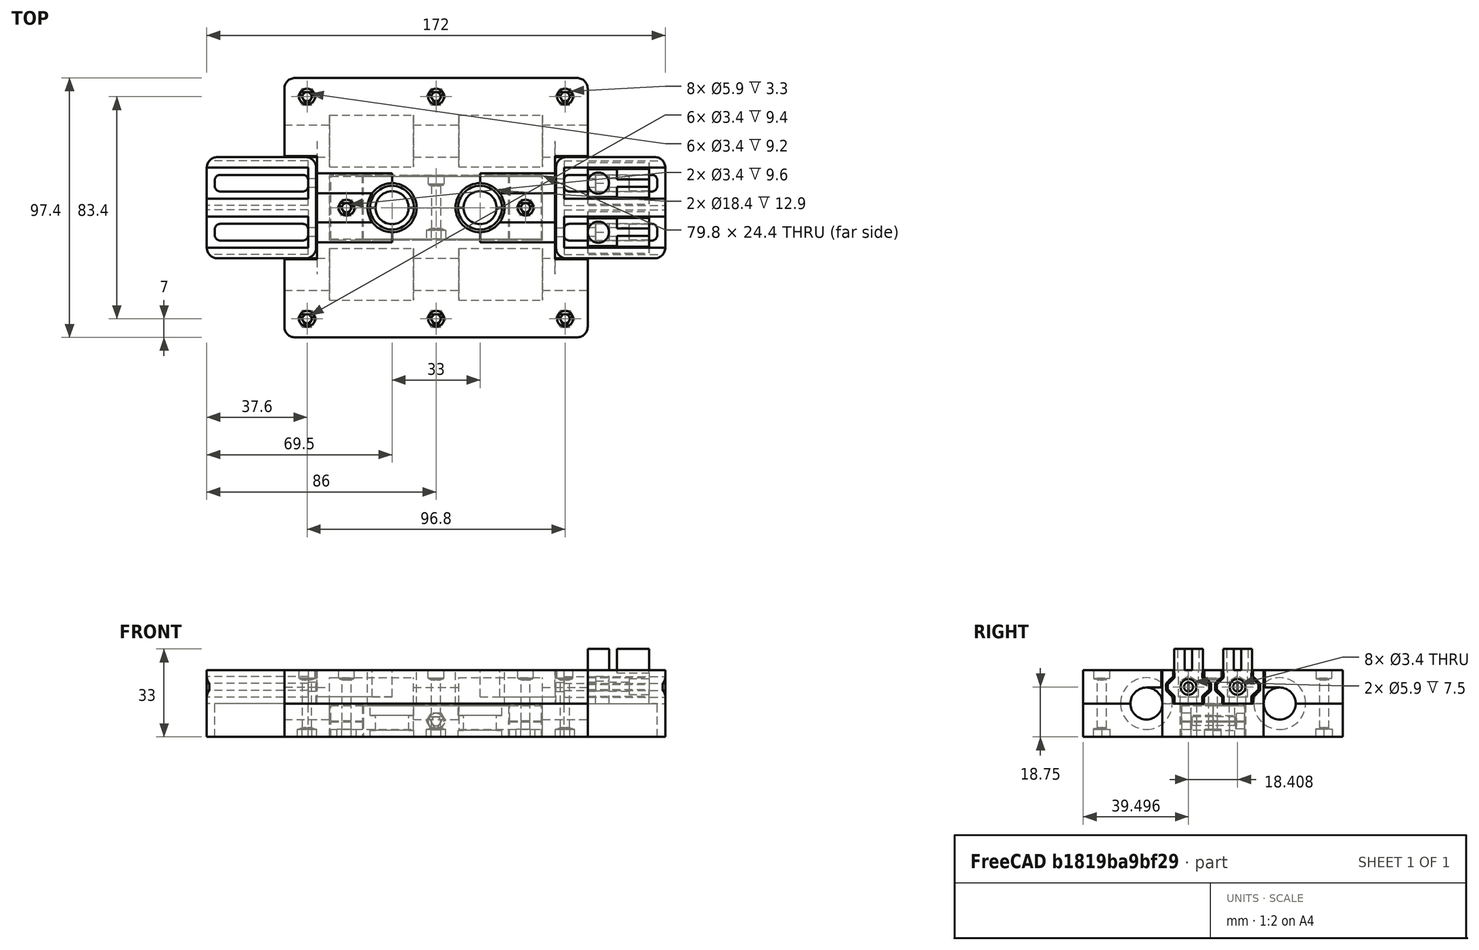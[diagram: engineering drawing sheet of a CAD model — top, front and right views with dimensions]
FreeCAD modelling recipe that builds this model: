
FCSTD DOCUMENT  (FreeCAD 0.16R6706 (Git))
Label: carriage
License: All rights reserved
LicenseURL: http://en.wikipedia.org/wiki/All_rights_reserved
objects: Part::Prism×50, Part::Cylinder×49, Part::MultiFuse×35, Part::Box×27, Part::Common×16, Part::Cut×9, Part::Fillet×5, Part::Fuse×4, Part::Polygon×4, Part::Extrusion×4, Part::FeaturePython×4
note: 207 computed .brp shape members not serialized (recipe doc carries the construction recipe); baked Part::Feature solids carry a one-line shape summary decoded from their .brp

FEATURE [Part::Cylinder] extr_outup
  Angle = 360
  Height = 3.7
  Placement = pos=(0,0,8) rot=(0,0,1;0rad)
  Radius = 8.2
FEATURE [Part::Cylinder] extr_outup_2
  Angle = 360
  Height = 3.7
  Placement = pos=(0,0,8) rot=(0,0,1;0rad)
  Radius = 8.2
FEATURE [Part::Cylinder] extr_in
  Angle = 360
  Height = 5.6
  Placement = pos=(0,0,2.4) rot=(0,0,1;0rad)
  Radius = 6.2
FEATURE [Part::Cylinder] extr_in_2
  Angle = 360
  Height = 5.6
  Placement = pos=(0,0,2.4) rot=(0,0,1;0rad)
  Radius = 6.2
FEATURE [Part::Cylinder] extr_outbot
  Angle = 360
  Height = 3.4
  Placement = pos=(0,0,-1) rot=(0,0,1;0rad)
  Radius = 8.2
FEATURE [Part::Cylinder] extr_outbot_2
  Angle = 360
  Height = 3.4
  Placement = pos=(0,0,-1) rot=(0,0,1;0rad)
  Radius = 8.2
FEATURE [Part::MultiFuse] extr_rings_1
  Placement = pos=(16.5,0,0) rot=(0,0,1;0rad)
  Shapes = -> [extr_outup,extr_in,extr_outbot]
FEATURE [Part::MultiFuse] extr_rings_2
  Placement = pos=(-16.5,0,0) rot=(0,0,1;0rad)
  Shapes = -> [extr_outup_2,extr_in_2,extr_outbot_2]
FEATURE [Part::Box] extr_hold_1
  Height = 11.7
  Length = 79
  Placement = pos=(-39.5,0,0) rot=(0,0,1;0rad)
  Width = 11.8
FEATURE [Part::Box] extr_hold_2
  Height = 11.7
  Length = 79
  Placement = pos=(-39.5,-11.8,0) rot=(0,0,1;0rad)
  Width = 11.8
FEATURE [Part::Box] extr_hold_tab0
  Height = 5.65
  Length = 11.84
  Placement = pos=(-39.5,-1,6.05) rot=(0,0,1;0rad)
  Width = 12.8
FEATURE [Part::Box] extr_hold_tab0_hole
  Height = 7.05
  Length = 13.24
  Placement = pos=(-40.5,0,5.65) rot=(0,0,1;0rad)
  Width = 12.8
FEATURE [Part::Box] extr_hold_tab1
  Height = 5.65
  Length = 11.84
  Placement = pos=(-39.5,-11.8,0) rot=(0,0,1;0rad)
  Width = 12.8
FEATURE [Part::Box] extr_hold_tab1_hole
  Height = 7.05
  Length = 13.24
  Placement = pos=(-40.5,-12.8,-1) rot=(0,0,1;0rad)
  Width = 12.8
FEATURE [Part::Box] extr_hold_tab2
  Height = 5.65
  Length = 11.84
  Placement = pos=(27.66,-11.8,6.05) rot=(0,0,1;0rad)
  Width = 12.8
FEATURE [Part::Box] extr_hold_tab2_hole
  Height = 7.05
  Length = 13.24
  Placement = pos=(27.26,-12.8,5.65) rot=(0,0,1;0rad)
  Width = 12.8
FEATURE [Part::Box] extr_hold_tab3
  Height = 5.65
  Length = 11.84
  Placement = pos=(27.66,-1,0) rot=(0,0,1;0rad)
  Width = 12.8
FEATURE [Part::Box] extr_hold_tab3_hole
  Height = 7.05
  Length = 13.24
  Placement = pos=(27.26,0,-1) rot=(0,0,1;0rad)
  Width = 12.8
FEATURE [Part::MultiFuse] extr_hold1_holes_joint
  Shapes = -> [extr_hold_tab0_hole,extr_hold_tab3_hole]
FEATURE [Part::MultiFuse] extr_hold1_tabs_joint
  Shapes = -> [extr_hold_1,extr_hold_tab1,extr_hold_tab2]
FEATURE [Part::Cut] extr_hold1_joint
  Base = -> extr_hold1_tabs_joint
  Tool = -> extr_hold1_holes_joint
FEATURE [Part::MultiFuse] extr_hold2_holes_joint
  Shapes = -> [extr_hold_tab1_hole,extr_hold_tab2_hole]
FEATURE [Part::MultiFuse] extr_hold2_tabs_joint
  Shapes = -> [extr_hold_2,extr_hold_tab0,extr_hold_tab3]
FEATURE [Part::Cut] extr_hold2_joint
  Base = -> extr_hold2_tabs_joint
  Tool = -> extr_hold2_holes_joint
FEATURE [Part::Box] carlow_box
  Height = 12.5
  Length = 113.8
  Placement = pos=(-56.9,-48.7,0) rot=(0,0,1;0rad)
  Width = 97.4
FEATURE [Part::Fillet] carlow_box_fllt
  Base = -> carlow_box
  Edges = 4 edges r=4: [Edge1,Edge3,Edge5,Edge7]
FEATURE [Part::Box] carhig_box
  Height = 12.5
  Length = 113.8
  Placement = pos=(-56.9,-48.7,0) rot=(0,0,1;0rad)
  Width = 97.4
FEATURE [Part::Fillet] carhig_box_fllt
  Base = -> carhig_box
  Edges = 4 edges r=4: [Edge1,Edge3,Edge5,Edge7]
  Placement = pos=(0,0,12.5) rot=(0,0,1;0rad)
FEATURE [Part::Box] inrect
  Height = 14.5
  Length = 79.8
  Placement = pos=(-39.9,-12.2,-1) rot=(0,0,1;0rad)
  Width = 24.4
FEATURE [Part::Box] extrhold_higcar
  Height = 1.4
  Length = 79
  Placement = pos=(-39.5,-11.8,12.1) rot=(0,0,1;0rad)
  Width = 23.6
FEATURE [Part::Fuse] carghig_fuse
  Base = -> carhig_box_fllt
  Tool = -> extrhold_higcar
FEATURE [Part::Cylinder] rod_p
  Angle = 360
  Height = 115.8
  Placement = pos=(-57.9,25,12.5) rot=(0,1,0;1.5708rad)
  Radius = 6
FEATURE [Part::Cylinder] rod_n
  Angle = 360
  Height = 115.8
  Placement = pos=(-57.9,-25,12.5) rot=(0,1,0;1.5708rad)
  Radius = 6
FEATURE [Part::Cylinder] bearing_0
  Angle = 360
  Height = 31.4
  Placement = pos=(8.5,25,12.5) rot=(0,1,0;1.5708rad)
  Radius = 9.7
FEATURE [Part::Cylinder] bearing_1
  Angle = 360
  Height = 31.4
  Placement = pos=(-39.9,25,12.5) rot=(0,1,0;1.5708rad)
  Radius = 9.7
FEATURE [Part::Cylinder] bearing_2
  Angle = 360
  Height = 31.4
  Placement = pos=(8.5,-25,12.5) rot=(0,1,0;1.5708rad)
  Radius = 9.7
FEATURE [Part::Cylinder] bearing_3
  Angle = 360
  Height = 31.4
  Placement = pos=(-39.9,-25,12.5) rot=(0,1,0;1.5708rad)
  Radius = 9.7
FEATURE [Part::Cylinder] higcar_fil_hole1
  Angle = 360
  Height = 15.3
  Placement = pos=(16.5,0,10.7) rot=(0,0,1;0rad)
  Radius = 9.2
FEATURE [Part::Cylinder] higcar_fil_hole2
  Angle = 360
  Height = 15.3
  Placement = pos=(-16.5,0,10.7) rot=(0,0,1;0rad)
  Radius = 9.2
FEATURE [Part::Cylinder] m3_extrbolt_hole_bolt_shank
  Angle = 360
  Height = 25.6
  Placement = pos=(0,0,-1) rot=(0,0,1;0rad)
  Radius = 1.7
FEATURE [Part::Cylinder] m3_extrbolt_hole_bolt_head
  Angle = 360
  Height = 4
  Placement = pos=(0,0,-1) rot=(0,0,1;0rad)
  Radius = 2.95
FEATURE [Part::Prism] m3_extrbolt_hole_bolt_sup1
  Circumradius = 3.4
  Height = 3.3
  Placement = pos=(0,0,0) rot=(0,0,1;0.523599rad)
  Polygon = 3
FEATURE [Part::Cylinder] m3_extrbolt_hole_bolt_sup1away
  Angle = 360
  Height = 3.3
  Radius = 2.95
FEATURE [Part::Common] sup1cut
  Base = -> m3_extrbolt_hole_bolt_sup1
  Tool = -> m3_extrbolt_hole_bolt_sup1away
FEATURE [Part::Prism] m3_extrbolt_hole_bolt_sup2
  Circumradius = 1.955
  Height = 3.6
  Polygon = 6
FEATURE [Part::MultiFuse] m3_extrbolt_hole_bolt
  Shapes = -> [m3_extrbolt_hole_bolt_shank,m3_extrbolt_hole_bolt_head,sup1cut,m3_extrbolt_hole_bolt_sup2]
FEATURE [Part::Prism] m3_extrbolt_hole_nut
  Circumradius = 3.605
  Height = 4.4
  Placement = pos=(0,0,20.2) rot=(0,0,1;0rad)
  Polygon = 6
FEATURE [Part::Prism] m3_extrbolt_hole_nutsup1
  Circumradius = 3.4
  Height = 3.7
  Placement = pos=(0,0,19.9) rot=(0,0,1;0.523599rad)
  Polygon = 3
FEATURE [Part::Prism] m3_extrbolt_hole_supnut1away
  Circumradius = 3.605
  Height = 3.7
  Placement = pos=(0,0,19.9) rot=(0,0,1;0rad)
  Polygon = 6
FEATURE [Part::Common] supnut1_cut
  Base = -> m3_extrbolt_hole_nutsup1
  Tool = -> m3_extrbolt_hole_supnut1away
FEATURE [Part::Prism] m3_extrbolt_hole_supnut2
  Circumradius = 1.955
  Height = 4
  Placement = pos=(0,0,19.6) rot=(0,0,1;0rad)
  Polygon = 6
FEATURE [Part::MultiFuse] boltnut
  Placement = pos=(0,11.8,5.85) rot=(1,0,0;1.5708rad)
  Shapes = -> [m3_extrbolt_hole_bolt,m3_extrbolt_hole_nut,supnut1_cut,m3_extrbolt_hole_supnut2]
FEATURE [Part::Cylinder] m3_bolt_hole_bolt_shank
  Angle = 360
  Height = 27
  Placement = pos=(0,0,-1) rot=(0,0,1;0rad)
  Radius = 1.7
FEATURE [Part::Cylinder] m3_bolt_hole_bolt_head
  Angle = 360
  Height = 4
  Placement = pos=(0,0,22) rot=(0,0,1;0rad)
  Radius = 2.95
FEATURE [Part::Prism] m3_bolt_hole_bolt_sup1
  Circumradius = 3.4
  Height = 3.3
  Placement = pos=(0,0,21.7) rot=(0,0,1;0.523599rad)
  Polygon = 3
FEATURE [Part::Cylinder] m3_bolt_hole_bolt_sup1away
  Angle = 360
  Height = 3.3
  Placement = pos=(0,0,21.7) rot=(0,0,1;0rad)
  Radius = 2.95
FEATURE [Part::Common] sup1cut001
  Base = -> m3_bolt_hole_bolt_sup1
  Tool = -> m3_bolt_hole_bolt_sup1away
FEATURE [Part::Prism] m3_bolt_hole_bolt_sup2
  Circumradius = 1.955
  Height = 3.6
  Placement = pos=(0,0,21.4) rot=(0,0,1;0rad)
  Polygon = 6
FEATURE [Part::MultiFuse] m3_bolt_hole_bolt
  Shapes = -> [m3_bolt_hole_bolt_shank,m3_bolt_hole_bolt_head,sup1cut001,m3_bolt_hole_bolt_sup2]
FEATURE [Part::Prism] m3_bolt_hole_nut
  Circumradius = 3.605
  Height = 3.8
  Placement = pos=(0,0,-1) rot=(0,0,1;0rad)
  Polygon = 6
FEATURE [Part::MultiFuse] boltnut001
  Placement = pos=(33.58,0,0) rot=(0,0,1;0rad)
  Shapes = -> [m3_bolt_hole_bolt,m3_bolt_hole_nut]
FEATURE [Part::Cylinder] m3_bolt_hole_bolt_shank001
  Angle = 360
  Height = 27
  Placement = pos=(0,0,-1) rot=(0,0,1;0rad)
  Radius = 1.7
FEATURE [Part::Cylinder] m3_bolt_hole_bolt_head001
  Angle = 360
  Height = 4
  Placement = pos=(0,0,22) rot=(0,0,1;0rad)
  Radius = 2.95
FEATURE [Part::Prism] m3_bolt_hole_bolt_sup1001
  Circumradius = 3.4
  Height = 3.3
  Placement = pos=(0,0,21.7) rot=(0,0,1;0.523599rad)
  Polygon = 3
FEATURE [Part::Cylinder] m3_bolt_hole_bolt_sup1away001
  Angle = 360
  Height = 3.3
  Placement = pos=(0,0,21.7) rot=(0,0,1;0rad)
  Radius = 2.95
FEATURE [Part::Common] sup1cut002
  Base = -> m3_bolt_hole_bolt_sup1001
  Tool = -> m3_bolt_hole_bolt_sup1away001
FEATURE [Part::Prism] m3_bolt_hole_bolt_sup2001
  Circumradius = 1.955
  Height = 3.6
  Placement = pos=(0,0,21.4) rot=(0,0,1;0rad)
  Polygon = 6
FEATURE [Part::MultiFuse] m3_bolt_hole_bolt001
  Shapes = -> [m3_bolt_hole_bolt_shank001,m3_bolt_hole_bolt_head001,sup1cut002,m3_bolt_hole_bolt_sup2001]
FEATURE [Part::Prism] m3_bolt_hole_nut001
  Circumradius = 3.605
  Height = 3.8
  Placement = pos=(0,0,-1) rot=(0,0,1;0rad)
  Polygon = 6
FEATURE [Part::MultiFuse] boltnut002
  Placement = pos=(-33.58,0,0) rot=(0,0,1;0rad)
  Shapes = -> [m3_bolt_hole_bolt001,m3_bolt_hole_nut001]
FEATURE [Part::Cylinder] m3_bolt_hole_bolt_shank002
  Angle = 360
  Height = 27
  Placement = pos=(0,0,-1) rot=(0,0,1;0rad)
  Radius = 1.7
FEATURE [Part::Cylinder] m3_bolt_hole_bolt_head002
  Angle = 360
  Height = 4
  Placement = pos=(0,0,22) rot=(0,0,1;0rad)
  Radius = 2.95
FEATURE [Part::Prism] m3_bolt_hole_bolt_sup1002
  Circumradius = 3.4
  Height = 3.3
  Placement = pos=(0,0,21.7) rot=(0,0,1;0.523599rad)
  Polygon = 3
FEATURE [Part::Cylinder] m3_bolt_hole_bolt_sup1away002
  Angle = 360
  Height = 3.3
  Placement = pos=(0,0,21.7) rot=(0,0,1;0rad)
  Radius = 2.95
FEATURE [Part::Common] sup1cut003
  Base = -> m3_bolt_hole_bolt_sup1002
  Tool = -> m3_bolt_hole_bolt_sup1away002
FEATURE [Part::Prism] m3_bolt_hole_bolt_sup2002
  Circumradius = 1.955
  Height = 3.6
  Placement = pos=(0,0,21.4) rot=(0,0,1;0rad)
  Polygon = 6
FEATURE [Part::MultiFuse] m3_bolt_hole_bolt002
  Shapes = -> [m3_bolt_hole_bolt_shank002,m3_bolt_hole_bolt_head002,sup1cut003,m3_bolt_hole_bolt_sup2002]
FEATURE [Part::Prism] m3_bolt_hole_nut002
  Circumradius = 3.605
  Height = 3.8
  Placement = pos=(0,0,-1) rot=(0,0,1;0rad)
  Polygon = 6
FEATURE [Part::Prism] m3_bolt_hole_nutsup1
  Circumradius = 3.4
  Height = 3.1
  Placement = pos=(0,0,0) rot=(0,0,1;0.523599rad)
  Polygon = 3
FEATURE [Part::Prism] m3_bolt_hole_supnut1away
  Circumradius = 3.605
  Height = 3.1
  Polygon = 6
FEATURE [Part::Common] supnut1_cut001
  Base = -> m3_bolt_hole_nutsup1
  Tool = -> m3_bolt_hole_supnut1away
FEATURE [Part::Prism] m3_bolt_hole_supnut2
  Circumradius = 1.955
  Height = 3.4
  Polygon = 6
FEATURE [Part::MultiFuse] boltnut003
  Placement = pos=(48.4,41.7,0) rot=(0,0,1;0rad)
  Shapes = -> [m3_bolt_hole_bolt002,m3_bolt_hole_nut002,supnut1_cut001,m3_bolt_hole_supnut2]
FEATURE [Part::Cylinder] m3_bolt_hole_bolt_shank003
  Angle = 360
  Height = 27
  Placement = pos=(0,0,-1) rot=(0,0,1;0rad)
  Radius = 1.7
FEATURE [Part::Cylinder] m3_bolt_hole_bolt_head003
  Angle = 360
  Height = 4
  Placement = pos=(0,0,22) rot=(0,0,1;0rad)
  Radius = 2.95
FEATURE [Part::Prism] m3_bolt_hole_bolt_sup1003
  Circumradius = 3.4
  Height = 3.3
  Placement = pos=(0,0,21.7) rot=(0,0,1;0.523599rad)
  Polygon = 3
FEATURE [Part::Cylinder] m3_bolt_hole_bolt_sup1away003
  Angle = 360
  Height = 3.3
  Placement = pos=(0,0,21.7) rot=(0,0,1;0rad)
  Radius = 2.95
FEATURE [Part::Common] sup1cut004
  Base = -> m3_bolt_hole_bolt_sup1003
  Tool = -> m3_bolt_hole_bolt_sup1away003
FEATURE [Part::Prism] m3_bolt_hole_bolt_sup2003
  Circumradius = 1.955
  Height = 3.6
  Placement = pos=(0,0,21.4) rot=(0,0,1;0rad)
  Polygon = 6
FEATURE [Part::MultiFuse] m3_bolt_hole_bolt003
  Shapes = -> [m3_bolt_hole_bolt_shank003,m3_bolt_hole_bolt_head003,sup1cut004,m3_bolt_hole_bolt_sup2003]
FEATURE [Part::Prism] m3_bolt_hole_nut003
  Circumradius = 3.605
  Height = 3.8
  Placement = pos=(0,0,-1) rot=(0,0,1;0rad)
  Polygon = 6
FEATURE [Part::Prism] m3_bolt_hole_nutsup1001
  Circumradius = 3.4
  Height = 3.1
  Placement = pos=(0,0,0) rot=(0,0,1;0.523599rad)
  Polygon = 3
FEATURE [Part::Prism] m3_bolt_hole_supnut1away001
  Circumradius = 3.605
  Height = 3.1
  Polygon = 6
FEATURE [Part::Common] supnut1_cut002
  Base = -> m3_bolt_hole_nutsup1001
  Tool = -> m3_bolt_hole_supnut1away001
FEATURE [Part::Prism] m3_bolt_hole_supnut2001
  Circumradius = 1.955
  Height = 3.4
  Polygon = 6
FEATURE [Part::MultiFuse] boltnut004
  Placement = pos=(0,41.7,0) rot=(0,0,1;0rad)
  Shapes = -> [m3_bolt_hole_bolt003,m3_bolt_hole_nut003,supnut1_cut002,m3_bolt_hole_supnut2001]
FEATURE [Part::Cylinder] m3_bolt_hole_bolt_shank004
  Angle = 360
  Height = 27
  Placement = pos=(0,0,-1) rot=(0,0,1;0rad)
  Radius = 1.7
FEATURE [Part::Cylinder] m3_bolt_hole_bolt_head004
  Angle = 360
  Height = 4
  Placement = pos=(0,0,22) rot=(0,0,1;0rad)
  Radius = 2.95
FEATURE [Part::Prism] m3_bolt_hole_bolt_sup1004
  Circumradius = 3.4
  Height = 3.3
  Placement = pos=(0,0,21.7) rot=(0,0,1;0.523599rad)
  Polygon = 3
FEATURE [Part::Cylinder] m3_bolt_hole_bolt_sup1away004
  Angle = 360
  Height = 3.3
  Placement = pos=(0,0,21.7) rot=(0,0,1;0rad)
  Radius = 2.95
FEATURE [Part::Common] sup1cut005
  Base = -> m3_bolt_hole_bolt_sup1004
  Tool = -> m3_bolt_hole_bolt_sup1away004
FEATURE [Part::Prism] m3_bolt_hole_bolt_sup2004
  Circumradius = 1.955
  Height = 3.6
  Placement = pos=(0,0,21.4) rot=(0,0,1;0rad)
  Polygon = 6
FEATURE [Part::MultiFuse] m3_bolt_hole_bolt004
  Shapes = -> [m3_bolt_hole_bolt_shank004,m3_bolt_hole_bolt_head004,sup1cut005,m3_bolt_hole_bolt_sup2004]
FEATURE [Part::Prism] m3_bolt_hole_nut004
  Circumradius = 3.605
  Height = 3.8
  Placement = pos=(0,0,-1) rot=(0,0,1;0rad)
  Polygon = 6
FEATURE [Part::Prism] m3_bolt_hole_nutsup1002
  Circumradius = 3.4
  Height = 3.1
  Placement = pos=(0,0,0) rot=(0,0,1;0.523599rad)
  Polygon = 3
FEATURE [Part::Prism] m3_bolt_hole_supnut1away002
  Circumradius = 3.605
  Height = 3.1
  Polygon = 6
FEATURE [Part::Common] supnut1_cut003
  Base = -> m3_bolt_hole_nutsup1002
  Tool = -> m3_bolt_hole_supnut1away002
FEATURE [Part::Prism] m3_bolt_hole_supnut2002
  Circumradius = 1.955
  Height = 3.4
  Polygon = 6
FEATURE [Part::MultiFuse] boltnut005
  Placement = pos=(-48.4,41.7,0) rot=(0,0,1;0rad)
  Shapes = -> [m3_bolt_hole_bolt004,m3_bolt_hole_nut004,supnut1_cut003,m3_bolt_hole_supnut2002]
FEATURE [Part::Cylinder] m3_bolt_hole_bolt_shank005
  Angle = 360
  Height = 27
  Placement = pos=(0,0,-1) rot=(0,0,1;0rad)
  Radius = 1.7
FEATURE [Part::Cylinder] m3_bolt_hole_bolt_head005
  Angle = 360
  Height = 4
  Placement = pos=(0,0,22) rot=(0,0,1;0rad)
  Radius = 2.95
FEATURE [Part::Prism] m3_bolt_hole_bolt_sup1005
  Circumradius = 3.4
  Height = 3.3
  Placement = pos=(0,0,21.7) rot=(0,0,1;0.523599rad)
  Polygon = 3
FEATURE [Part::Cylinder] m3_bolt_hole_bolt_sup1away005
  Angle = 360
  Height = 3.3
  Placement = pos=(0,0,21.7) rot=(0,0,1;0rad)
  Radius = 2.95
FEATURE [Part::Common] sup1cut006
  Base = -> m3_bolt_hole_bolt_sup1005
  Tool = -> m3_bolt_hole_bolt_sup1away005
FEATURE [Part::Prism] m3_bolt_hole_bolt_sup2005
  Circumradius = 1.955
  Height = 3.6
  Placement = pos=(0,0,21.4) rot=(0,0,1;0rad)
  Polygon = 6
FEATURE [Part::MultiFuse] m3_bolt_hole_bolt005
  Shapes = -> [m3_bolt_hole_bolt_shank005,m3_bolt_hole_bolt_head005,sup1cut006,m3_bolt_hole_bolt_sup2005]
FEATURE [Part::Prism] m3_bolt_hole_nut005
  Circumradius = 3.605
  Height = 3.8
  Placement = pos=(0,0,-1) rot=(0,0,1;0rad)
  Polygon = 6
FEATURE [Part::Prism] m3_bolt_hole_nutsup1003
  Circumradius = 3.4
  Height = 3.1
  Placement = pos=(0,0,0) rot=(0,0,1;0.523599rad)
  Polygon = 3
FEATURE [Part::Prism] m3_bolt_hole_supnut1away003
  Circumradius = 3.605
  Height = 3.1
  Polygon = 6
FEATURE [Part::Common] supnut1_cut004
  Base = -> m3_bolt_hole_nutsup1003
  Tool = -> m3_bolt_hole_supnut1away003
FEATURE [Part::Prism] m3_bolt_hole_supnut2003
  Circumradius = 1.955
  Height = 3.4
  Polygon = 6
FEATURE [Part::MultiFuse] boltnut006
  Placement = pos=(48.4,-41.7,0) rot=(0,0,1;0rad)
  Shapes = -> [m3_bolt_hole_bolt005,m3_bolt_hole_nut005,supnut1_cut004,m3_bolt_hole_supnut2003]
FEATURE [Part::Cylinder] m3_bolt_hole_bolt_shank006
  Angle = 360
  Height = 27
  Placement = pos=(0,0,-1) rot=(0,0,1;0rad)
  Radius = 1.7
FEATURE [Part::Cylinder] m3_bolt_hole_bolt_head006
  Angle = 360
  Height = 4
  Placement = pos=(0,0,22) rot=(0,0,1;0rad)
  Radius = 2.95
FEATURE [Part::Prism] m3_bolt_hole_bolt_sup1006
  Circumradius = 3.4
  Height = 3.3
  Placement = pos=(0,0,21.7) rot=(0,0,1;0.523599rad)
  Polygon = 3
FEATURE [Part::Cylinder] m3_bolt_hole_bolt_sup1away006
  Angle = 360
  Height = 3.3
  Placement = pos=(0,0,21.7) rot=(0,0,1;0rad)
  Radius = 2.95
FEATURE [Part::Common] sup1cut007
  Base = -> m3_bolt_hole_bolt_sup1006
  Tool = -> m3_bolt_hole_bolt_sup1away006
FEATURE [Part::Prism] m3_bolt_hole_bolt_sup2006
  Circumradius = 1.955
  Height = 3.6
  Placement = pos=(0,0,21.4) rot=(0,0,1;0rad)
  Polygon = 6
FEATURE [Part::MultiFuse] m3_bolt_hole_bolt006
  Shapes = -> [m3_bolt_hole_bolt_shank006,m3_bolt_hole_bolt_head006,sup1cut007,m3_bolt_hole_bolt_sup2006]
FEATURE [Part::Prism] m3_bolt_hole_nut006
  Circumradius = 3.605
  Height = 3.8
  Placement = pos=(0,0,-1) rot=(0,0,1;0rad)
  Polygon = 6
FEATURE [Part::Prism] m3_bolt_hole_nutsup1004
  Circumradius = 3.4
  Height = 3.1
  Placement = pos=(0,0,0) rot=(0,0,1;0.523599rad)
  Polygon = 3
FEATURE [Part::Prism] m3_bolt_hole_supnut1away004
  Circumradius = 3.605
  Height = 3.1
  Polygon = 6
FEATURE [Part::Common] supnut1_cut005
  Base = -> m3_bolt_hole_nutsup1004
  Tool = -> m3_bolt_hole_supnut1away004
FEATURE [Part::Prism] m3_bolt_hole_supnut2004
  Circumradius = 1.955
  Height = 3.4
  Polygon = 6
FEATURE [Part::MultiFuse] boltnut007
  Placement = pos=(0,-41.7,0) rot=(0,0,1;0rad)
  Shapes = -> [m3_bolt_hole_bolt006,m3_bolt_hole_nut006,supnut1_cut005,m3_bolt_hole_supnut2004]
FEATURE [Part::Cylinder] m3_bolt_hole_bolt_shank007
  Angle = 360
  Height = 27
  Placement = pos=(0,0,-1) rot=(0,0,1;0rad)
  Radius = 1.7
FEATURE [Part::Cylinder] m3_bolt_hole_bolt_head007
  Angle = 360
  Height = 4
  Placement = pos=(0,0,22) rot=(0,0,1;0rad)
  Radius = 2.95
FEATURE [Part::Prism] m3_bolt_hole_bolt_sup1007
  Circumradius = 3.4
  Height = 3.3
  Placement = pos=(0,0,21.7) rot=(0,0,1;0.523599rad)
  Polygon = 3
FEATURE [Part::Cylinder] m3_bolt_hole_bolt_sup1away007
  Angle = 360
  Height = 3.3
  Placement = pos=(0,0,21.7) rot=(0,0,1;0rad)
  Radius = 2.95
FEATURE [Part::Common] sup1cut008
  Base = -> m3_bolt_hole_bolt_sup1007
  Tool = -> m3_bolt_hole_bolt_sup1away007
FEATURE [Part::Prism] m3_bolt_hole_bolt_sup2007
  Circumradius = 1.955
  Height = 3.6
  Placement = pos=(0,0,21.4) rot=(0,0,1;0rad)
  Polygon = 6
FEATURE [Part::MultiFuse] m3_bolt_hole_bolt007
  Shapes = -> [m3_bolt_hole_bolt_shank007,m3_bolt_hole_bolt_head007,sup1cut008,m3_bolt_hole_bolt_sup2007]
FEATURE [Part::Prism] m3_bolt_hole_nut007
  Circumradius = 3.605
  Height = 3.8
  Placement = pos=(0,0,-1) rot=(0,0,1;0rad)
  Polygon = 6
FEATURE [Part::Prism] m3_bolt_hole_nutsup1005
  Circumradius = 3.4
  Height = 3.1
  Placement = pos=(0,0,0) rot=(0,0,1;0.523599rad)
  Polygon = 3
FEATURE [Part::Prism] m3_bolt_hole_supnut1away005
  Circumradius = 3.605
  Height = 3.1
  Polygon = 6
FEATURE [Part::Common] supnut1_cut006
  Base = -> m3_bolt_hole_nutsup1005
  Tool = -> m3_bolt_hole_supnut1away005
FEATURE [Part::Prism] m3_bolt_hole_supnut2005
  Circumradius = 1.955
  Height = 3.4
  Polygon = 6
FEATURE [Part::MultiFuse] boltnut008
  Placement = pos=(-48.4,-41.7,0) rot=(0,0,1;0rad)
  Shapes = -> [m3_bolt_hole_bolt007,m3_bolt_hole_nut007,supnut1_cut006,m3_bolt_hole_supnut2005]
FEATURE [Part::Box] gt2clamp0_cb1
  Height = 9
  Length = 12
  Placement = pos=(11,2.60417,11.5) rot=(0,0,1;0rad)
  Width = 4
FEATURE [Part::Box] gt2clamp0_cb3
  Height = 9
  Length = 12
  Placement = pos=(11,9.40417,11.5) rot=(0,0,1;0rad)
  Width = 4
FEATURE [Part::Cylinder] gt2clamp0_cyl
  Angle = 360
  Height = 9
  Placement = pos=(4,8.00417,11.5) rot=(0,0,1;0rad)
  Radius = 4
FEATURE [Part::Polygon] gt2clamp0base_plane_yz
  Close = true
  Nodes = (12) [(0,2.80417,0),(0,2.80417,2.74375),(0,0.2,5.34792),(0,0.2,7.15208),(0,2.80417,9.75625),(0,2.80417,12.5),(0,13.2042,12.5),(0,13.2042,9.75625),+4 more]
FEATURE [Part::Extrusion] gt2clamp0extr_base
  Base = -> gt2clamp0base_plane_yz
  Dir = (23,0,0)
  Solid = true
FEATURE [Part::MultiFuse] gt2clamp0clamp_base
  Shapes = -> [gt2clamp0_cb1,gt2clamp0_cb3,gt2clamp0_cyl,gt2clamp0extr_base]
FEATURE [Part::Polygon] gt2clamp0_baseof_plane_yz
  Close = true
  Nodes = (12) [(0,2.20417,0),(0,2.20417,2.34375),(0,-0.4,4.94792),(0,-0.4,7.55208),(0,2.20417,10.1562),(0,2.20417,12.5),(0,13.8042,12.5),(0,13.8042,10.1562),+4 more]
FEATURE [Part::Extrusion] gt2clamp0_baseof
  Base = -> gt2clamp0_baseof_plane_yz
  Dir = (39,0,0)
  Placement = pos=(48,1.2,12.5) rot=(0,0,1;0rad)
  Solid = true
FEATURE [Part::Cylinder] gt2clamp0_base_lscrew_shank
  Angle = 360
  Height = 25
  Placement = pos=(0,0,-1) rot=(0,0,1;0rad)
  Radius = 1.7
FEATURE [Part::Cylinder] gt2clamp0_base_lscrew_head
  Angle = 360
  Height = 8.5
  Placement = pos=(0,0,-1) rot=(0,0,1;0rad)
  Radius = 2.95
FEATURE [Part::MultiFuse] gt2clamp0_base_lscrew
  Placement = pos=(23,8.00417,6.25) rot=(0,-1,0;1.5708rad)
  Shapes = -> [gt2clamp0_base_lscrew_shank,gt2clamp0_base_lscrew_head]
FEATURE [Part::Prism] gt2clamp0_base_lscrew_nut
  Circumradius = 3.605
  Height = 5.04
  Placement = pos=(3,8.00417,6.65) rot=(0,1,0;1.5708rad)
  Polygon = 6
FEATURE [Part::Box] gt2clamp0_base_lscrew_nut2
  Height = 6.65
  Length = 5.04
  Placement = pos=(3,4.88224,0) rot=(0,0,1;0rad)
  Width = 6.24386
FEATURE [Part::MultiFuse] gt2clamp0_clamp_hole
  Shapes = -> [gt2clamp0_base_lscrew,gt2clamp0_base_lscrew_nut,gt2clamp0_base_lscrew_nut2]
FEATURE [Part::Cut] gt2clamp0
  Base = -> gt2clamp0clamp_base
  Placement = pos=(56.9,1.2,12.5) rot=(0,0,1;0rad)
  Tool = -> gt2clamp0_clamp_hole
FEATURE [Part::Box] gt2clamp1_cb1
  Height = 9
  Length = 12
  Placement = pos=(11,2.60417,11.5) rot=(0,0,1;0rad)
  Width = 4
FEATURE [Part::Box] gt2clamp1_cb3
  Height = 9
  Length = 12
  Placement = pos=(11,9.40417,11.5) rot=(0,0,1;0rad)
  Width = 4
FEATURE [Part::Cylinder] gt2clamp1_cyl
  Angle = 360
  Height = 9
  Placement = pos=(4,8.00417,11.5) rot=(0,0,1;0rad)
  Radius = 4
FEATURE [Part::Polygon] gt2clamp1base_plane_yz
  Close = true
  Nodes = (12) [(0,2.80417,0),(0,2.80417,2.74375),(0,0.2,5.34792),(0,0.2,7.15208),(0,2.80417,9.75625),(0,2.80417,12.5),(0,13.2042,12.5),(0,13.2042,9.75625),+4 more]
FEATURE [Part::Extrusion] gt2clamp1extr_base
  Base = -> gt2clamp1base_plane_yz
  Dir = (23,0,0)
  Solid = true
FEATURE [Part::MultiFuse] gt2clamp1clamp_base
  Shapes = -> [gt2clamp1_cb1,gt2clamp1_cb3,gt2clamp1_cyl,gt2clamp1extr_base]
FEATURE [Part::Polygon] gt2clamp1_baseof_plane_yz
  Close = true
  Nodes = (12) [(0,2.20417,0),(0,2.20417,2.34375),(0,-0.4,4.94792),(0,-0.4,7.55208),(0,2.20417,10.1562),(0,2.20417,12.5),(0,13.8042,12.5),(0,13.8042,10.1562),+4 more]
FEATURE [Part::Extrusion] gt2clamp1_baseof
  Base = -> gt2clamp1_baseof_plane_yz
  Dir = (39,0,0)
  Placement = pos=(48,-17.2083,12.5) rot=(0,0,1;0rad)
  Solid = true
FEATURE [Part::Cylinder] gt2clamp1_base_lscrew_shank
  Angle = 360
  Height = 25
  Placement = pos=(0,0,-1) rot=(0,0,1;0rad)
  Radius = 1.7
FEATURE [Part::Cylinder] gt2clamp1_base_lscrew_head
  Angle = 360
  Height = 8.5
  Placement = pos=(0,0,-1) rot=(0,0,1;0rad)
  Radius = 2.95
FEATURE [Part::MultiFuse] gt2clamp1_base_lscrew
  Placement = pos=(23,8.00417,6.25) rot=(0,-1,0;1.5708rad)
  Shapes = -> [gt2clamp1_base_lscrew_shank,gt2clamp1_base_lscrew_head]
FEATURE [Part::Prism] gt2clamp1_base_lscrew_nut
  Circumradius = 3.605
  Height = 5.04
  Placement = pos=(3,8.00417,6.65) rot=(0,1,0;1.5708rad)
  Polygon = 6
FEATURE [Part::Box] gt2clamp1_base_lscrew_nut2
  Height = 6.65
  Length = 5.04
  Placement = pos=(3,4.88224,0) rot=(0,0,1;0rad)
  Width = 6.24386
FEATURE [Part::MultiFuse] gt2clamp1_clamp_hole
  Shapes = -> [gt2clamp1_base_lscrew,gt2clamp1_base_lscrew_nut,gt2clamp1_base_lscrew_nut2]
FEATURE [Part::Cut] gt2clamp1
  Base = -> gt2clamp1clamp_base
  Placement = pos=(56.9,-17.2083,12.5) rot=(0,0,1;0rad)
  Tool = -> gt2clamp1_clamp_hole
FEATURE [Part::Box] bccr_box
  Height = 25
  Length = 41
  Placement = pos=(45,-19,0) rot=(0,0,1;0rad)
  Width = 38
FEATURE [Part::Fillet] bccr_fllt
  Base = -> bccr_box
  Edges = 4 edges r=4: [Edge1,Edge3,Edge5,Edge7]
FEATURE [Part::Box] bccr_box001
  Height = 25
  Length = 41
  Placement = pos=(44.6,-19.4,0) rot=(0,0,1;0rad)
  Width = 38.8
FEATURE [Part::Box] bccr_box_of_clean
  Height = 6
  Length = 41
  Placement = pos=(44.6,-25,12.5) rot=(0,0,1;0rad)
  Width = 50
FEATURE [Part::Fuse] fuse_bccr_box_of
  Base = -> bccr_box001
  Tool = -> bccr_box_of_clean
FEATURE [Part::FeaturePython] Clone  label="Clone of fuse_bccr_box_of"  # Draft clone (typed FeaturePython)
  Objects = -> [fuse_bccr_box_of]
  Placement = pos=(0,0,0) rot=(0,0,1;3.14159rad)
  Scale = (1,1,1)
FEATURE [Part::Box] highcar_lscrew_hole0
  Height = 11
  Length = 29.1
  Placement = pos=(16.5,5.45417,15) rot=(0,0,1;0rad)
  Width = 7.5
FEATURE [Part::Box] highcar_lscrew_hole1
  Height = 11
  Length = 29.1
  Placement = pos=(16.5,-12.9542,15) rot=(0,0,1;0rad)
  Width = 7.5
FEATURE [Part::Fuse] higcar_lscrew_fuse
  Base = -> highcar_lscrew_hole0
  Tool = -> highcar_lscrew_hole1
FEATURE [Part::FeaturePython] Clone001  label="Clone of higcar_lscrew_fuse"  # Draft clone (typed FeaturePython)
  Objects = -> [higcar_lscrew_fuse]
  Placement = pos=(0,0,0) rot=(0,0,1;3.14159rad)
  Scale = (1,1,1)
FEATURE [Part::Box] bccr_bthole0
  Height = 14.5
  Length = 35
  Placement = pos=(0,-3.12193,0) rot=(0,0,1;0rad)
  Width = 6.24386
FEATURE [Part::Fillet] bccr_bthole0_fllt
  Base = -> bccr_bthole0
  Edges = 4 edges r=2: [Edge1,Edge3,Edge5,Edge7]
  Placement = pos=(48,9.20417,-1) rot=(0,0,1;0rad)
FEATURE [Part::Box] bccr_bthole1
  Height = 14.5
  Length = 35
  Placement = pos=(0,-3.12193,0) rot=(0,0,1;0rad)
  Width = 6.24386
FEATURE [Part::Fillet] bccr_bthole1_fllt
  Base = -> bccr_bthole1
  Edges = 4 edges r=2: [Edge1,Edge3,Edge5,Edge7]
  Placement = pos=(48,-9.20417,-1) rot=(0,0,1;0rad)
FEATURE [Part::Fuse] bccr_bthole_fused
  Base = -> bccr_bthole0_fllt
  Tool = -> bccr_bthole1_fllt
FEATURE [Part::FeaturePython] Clone002  label="Clone of bccr_bthole_fused"  # Draft clone (typed FeaturePython)
  Objects = -> [bccr_bthole_fused]
  Placement = pos=(0,0,0) rot=(0,0,1;3.14159rad)
  Scale = (1,1,1)
FEATURE [Part::Cylinder] bccr_bolthole0
  Angle = 360
  Height = 5
  Placement = pos=(44,9.20417,18.75) rot=(0,1,0;1.5708rad)
  Radius = 1.7
FEATURE [Part::Cylinder] bccr_bolthole1
  Angle = 360
  Height = 5
  Placement = pos=(44,-9.20417,18.75) rot=(0,1,0;1.5708rad)
  Radius = 1.7
FEATURE [Part::MultiFuse] bccr_holes
  Shapes = -> [gt2clamp0_baseof,gt2clamp1_baseof,bccr_bthole0_fllt,bccr_bthole1_fllt,bccr_bolthole0,bccr_bolthole1]
FEATURE [Part::Cut] bccr_final
  Base = -> bccr_fllt
  Tool = -> bccr_holes
FEATURE [Part::FeaturePython] Clone003  label="Clone of bccr_final"  # Draft clone (typed FeaturePython)
  Objects = -> [bccr_final]
  Placement = pos=(0,0,0) rot=(0,0,1;3.14159rad)
  Scale = (1,1,1)
FEATURE [Part::MultiFuse] fuse_extr_holder_holes
  Shapes = -> [extr_rings_1,extr_rings_2,boltnut,boltnut001,boltnut002]
FEATURE [Part::Cut] tot_extr_hold_1
  Base = -> extr_hold1_joint
  Tool = -> fuse_extr_holder_holes
FEATURE [Part::Cut] tot_extr_hold_2
  Base = -> extr_hold2_joint
  Tool = -> fuse_extr_holder_holes
FEATURE [Part::MultiFuse] fuse_lowcar_holes
  Shapes = -> [inrect,rod_n,rod_p,bearing_0,bearing_1,bearing_2,bearing_3,boltnut003,boltnut004,boltnut005,boltnut006,boltnut007,boltnut008,bccr_bthole_fused,Clone002]
FEATURE [Part::MultiFuse] fuse_higcar_holes
  Shapes = -> [rod_n,rod_p,bearing_0,bearing_1,bearing_2,bearing_3,higcar_fil_hole1,higcar_fil_hole2,boltnut001,boltnut002,boltnut003,boltnut004,boltnut005,boltnut006,boltnut007,boltnut008,fuse_bccr_box_of,Clone,higcar_lscrew_fuse,Clone001]
FEATURE [Part::Cut] lowcar_hole
  Base = -> carlow_box_fllt
  Tool = -> fuse_lowcar_holes
FEATURE [Part::MultiFuse] lowcar_bccr
  Shapes = -> [lowcar_hole,bccr_final,Clone003]
FEATURE [Part::Cut] higcar_hole
  Base = -> carghig_fuse
  Tool = -> fuse_higcar_holes
